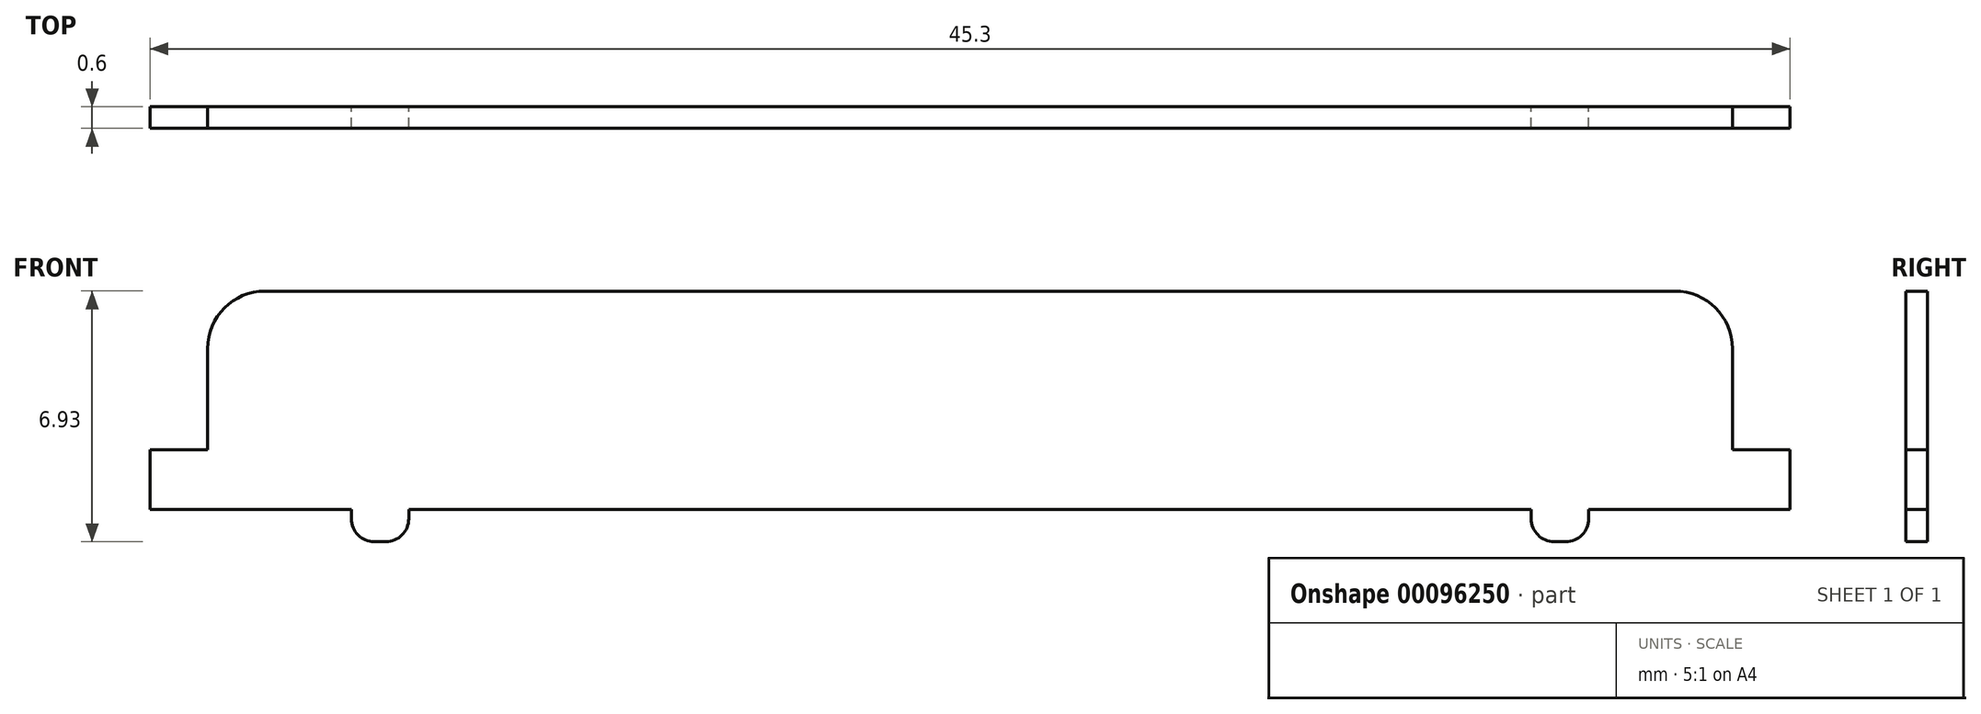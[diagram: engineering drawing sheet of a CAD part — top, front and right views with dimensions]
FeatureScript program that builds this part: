
annotation { "Feature Type Name" : "Feature", "Feature Type Description" : "" }
export const myFeature = defineFeature(function(context is Context, id is Id, definition is map)
    precondition{}
    {
        {
            assignVariable(context, id + "F0", {"name" : "fretwidth", "anyValue" : .6});
        }
        {
            var Q0;
            Q0=qCreatedBy(makeId("Front.planeOp"),FACE);
            var sketch = newSketch(context, id + "F1", { "sketchPlane" : qUnion([Q0])});
            skLineSegment(sketch, "E0", {"start": v(0, -3.2) * mm, "end": v(0, 3.25) * mm, "construction": true});
            skLineSegment(sketch, "E1", {"start": v(0, 0) * mm, "end": v(-15.5, 0) * mm});
            skLineSegment(sketch, "E2", {"start": v(-15.5, 0) * mm, "end": v(-15.5, -0.25) * mm});
            skLineSegment(sketch, "E3", {"start": v(-16.14, -0.89) * mm, "end": v(-16.46, -0.89) * mm});
            skLineSegment(sketch, "E4", {"start": v(-17.1, -0.25) * mm, "end": v(-17.1, 0) * mm});
            skLineSegment(sketch, "E5", {"start": v(-17.1, 0) * mm, "end": v(-22.65, 0) * mm});
            skLineSegment(sketch, "E6", {"start": v(-22.65, 0) * mm, "end": v(-22.65, 1.65) * mm});
            skLineSegment(sketch, "E7", {"start": v(-22.65, 1.65) * mm, "end": v(-21.06, 1.65) * mm});
            skLineSegment(sketch, "E8", {"start": v(-21.06, 1.65) * mm, "end": v(-21.06, 4.45) * mm});
            skLineSegment(sketch, "E9", {"start": v(-19.47, 6.04) * mm, "end": v(0, 6.04) * mm});
            skPoint(sketch, "E10.visualSharp", {"position": v(-21.06, 6.04) * mm});
            skArc(sketch, "E10.filletArc", {"start": v(-19.47, 6.04) * mm, "mid": v(-20.6, 5.57) * mm, "end": v(-21.06, 4.45) * mm});
            skPoint(sketch, "E11.visualSharp", {"position": v(-17.1, -0.89) * mm});
            skArc(sketch, "E11.filletArc", {"start": v(-17.1, -0.25) * mm, "mid": v(-16.9, -0.7) * mm, "end": v(-16.46, -0.89) * mm});
            skPoint(sketch, "E12.visualSharp", {"position": v(-15.5, -0.89) * mm});
            skArc(sketch, "E12.filletArc", {"start": v(-16.14, -0.89) * mm, "mid": v(-15.69, -0.7) * mm, "end": v(-15.5, -0.25) * mm});
            skLineSegment(sketch, "E13.MirrorCS", {"start": v(16.14, -0.89) * mm, "end": v(16.46, -0.89) * mm});
            skLineSegment(sketch, "E14.MirrorCS", {"start": v(15.5, 0) * mm, "end": v(15.5, -0.25) * mm});
            skLineSegment(sketch, "E15.MirrorCS", {"start": v(17.1, -0.25) * mm, "end": v(17.1, 0) * mm});
            skArc(sketch, "E16.MirrorCS", {"start": v(17.1, -0.25) * mm, "mid": v(16.9, -0.7) * mm, "end": v(16.46, -0.89) * mm});
            skArc(sketch, "E17.MirrorCS", {"start": v(16.14, -0.89) * mm, "mid": v(15.69, -0.7) * mm, "end": v(15.5, -0.25) * mm});
            skLineSegment(sketch, "E18.MirrorCS", {"start": v(19.47, 6.04) * mm, "end": v(0, 6.04) * mm});
            skLineSegment(sketch, "E19.MirrorCS", {"start": v(21.06, 1.65) * mm, "end": v(21.06, 4.45) * mm});
            skLineSegment(sketch, "E20.MirrorCS", {"start": v(22.65, 1.65) * mm, "end": v(21.06, 1.65) * mm});
            skLineSegment(sketch, "E21.MirrorCS", {"start": v(0, 0) * mm, "end": v(15.5, 0) * mm});
            skLineSegment(sketch, "E22.MirrorCS", {"start": v(22.65, 0) * mm, "end": v(22.65, 1.65) * mm});
            skPoint(sketch, "E23.MirrorP", {"position": v(15.5, -0.89) * mm});
            skArc(sketch, "E24.MirrorCS", {"start": v(19.47, 6.04) * mm, "mid": v(20.6, 5.57) * mm, "end": v(21.06, 4.45) * mm});
            skPoint(sketch, "E25.MirrorP", {"position": v(21.06, 6.04) * mm});
            skPoint(sketch, "E26.MirrorP", {"position": v(17.1, -0.89) * mm});
            skLineSegment(sketch, "E27.MirrorCS", {"start": v(17.1, 0) * mm, "end": v(22.65, 0) * mm});
            skLineSegment(sketch, "E28", {"start": v(-16.3, -0.55) * mm, "end": v(-16.3, -1.5) * mm, "construction": true});
            skPoint(sketch, "E28.startSnap0", {"position": v(-16.3, -0.89) * mm});
            skSolve(sketch);
        }
        {
            var Q0;
            Q0 = qSketchRegion(id + "F1", true);
            extrude(context, id + "F2", {"entities" : qUnion([Q0]), "depth" : (getVariable(context, 'fretwidth')) * mm});
        }
    });
